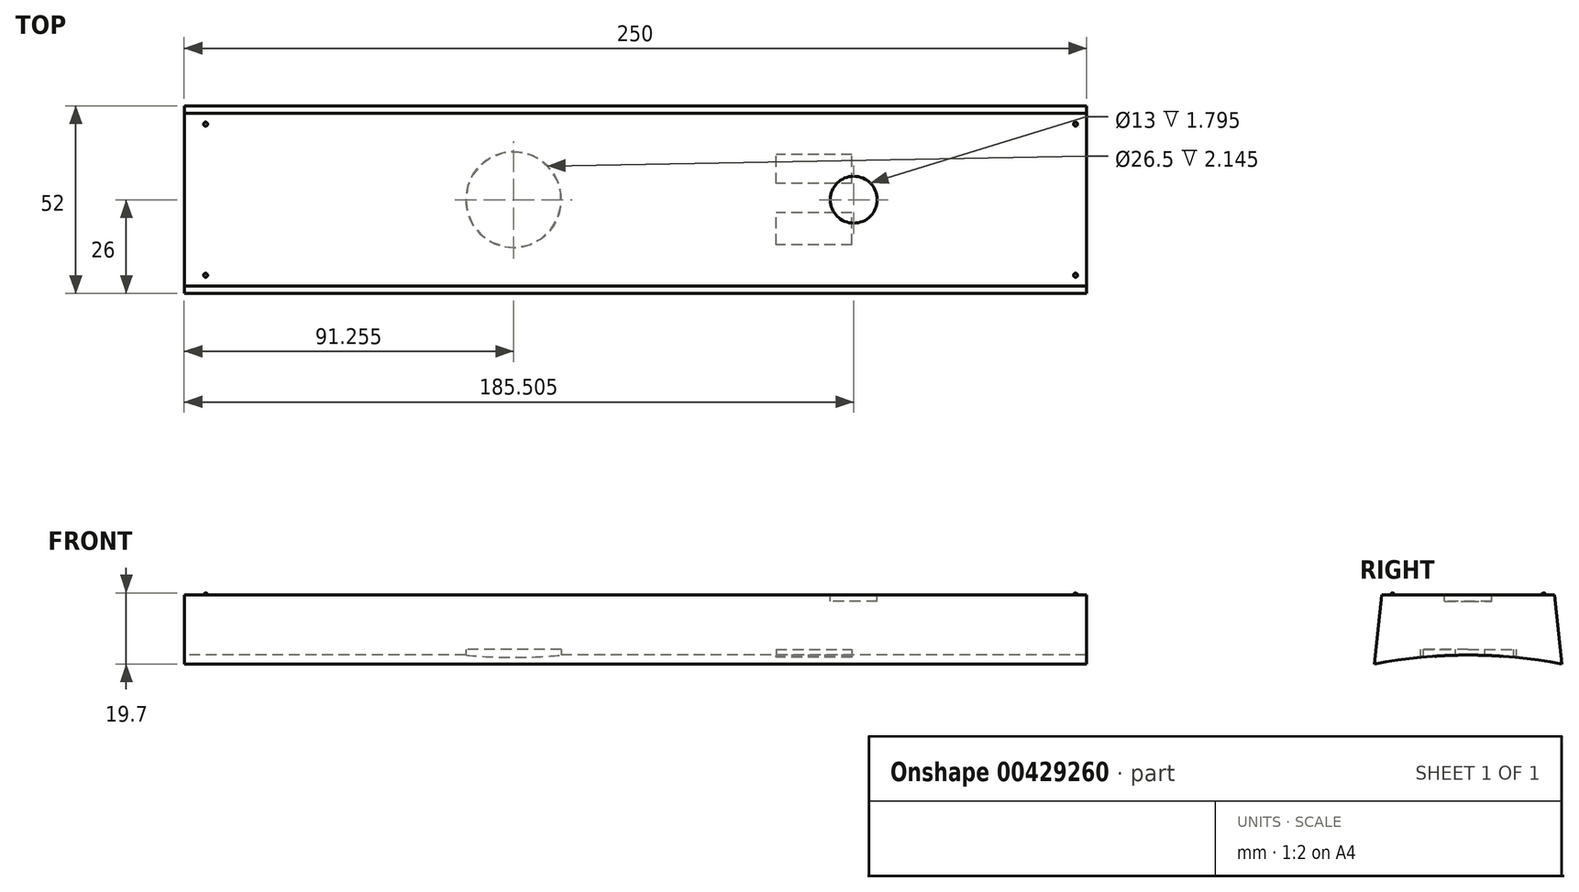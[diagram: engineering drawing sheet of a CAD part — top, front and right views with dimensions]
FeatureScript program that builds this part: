
annotation { "Feature Type Name" : "Feature", "Feature Type Description" : "" }
export const myFeature = defineFeature(function(context is Context, id is Id, definition is map)
    precondition{}
    {
        {
            var Q0;
            Q0=qCreatedBy(makeId("Top.planeOp"),FACE);
            var sketch = newSketch(context, id + "F0", { "sketchPlane" : qUnion([Q0])});
            skLineSegment(sketch, "E0.bottom", {"start": v(-126.45, 52) * mm, "end": v(123.55, 52) * mm});
            skLineSegment(sketch, "E0.top", {"start": v(-126.45, 0) * mm, "end": v(123.55, 0) * mm});
            skLineSegment(sketch, "E0.left", {"start": v(-126.45, 52) * mm, "end": v(-126.45, 0) * mm});
            skLineSegment(sketch, "E0.right", {"start": v(123.55, 52) * mm, "end": v(123.55, 0) * mm});
            skSolve(sketch);
        }
        {
            var Q0;
            Q0 = qSketchRegion(id + "F0", true);
            extrude(context, id + "F1", {"entities" : qUnion([Q0]), "depth" : 19.2 * mm});
        }
        {
            var Q0;
            Q0=makeQuery(id+"F1.opExtrude","CAP_EDGE",EDGE,{"disambiguationData":[OSD([sQuery(id+"F0.wireOp",EDGE,"E0.bottom")])],"isStart":false});
            chamfer(context, id + "F2", {"entities" : qUnion([Q0]), "chamferType" : ChamferType.OFFSET_ANGLE, "width" : 19.2 * mm, "oppositeDirection" : false, "angle" : 6 * degree, "tangentPropagation" : true});
        }
        {
            var Q0;
            Q0=makeQuery(id+"F1.opExtrude","CAP_EDGE",EDGE,{"disambiguationData":[OSD([sQuery(id+"F0.wireOp",EDGE,"E0.top")])],"isStart":false});
            chamfer(context, id + "F3", {"entities" : qUnion([Q0]), "chamferType" : ChamferType.OFFSET_ANGLE, "width" : 19.2 * mm, "oppositeDirection" : true, "angle" : 6 * degree, "tangentPropagation" : true});
        }
        {
            var Q0;
            Q0=makeQuery(id+"F1.opExtrude","CAP_FACE",FACE,{"disambiguationData":[OSD([sQuery(id+"F0.wireOp",EDGE,"E0.bottom"),sQuery(id+"F0.wireOp",EDGE,"E0.top"),sQuery(id+"F0.wireOp",EDGE,"E0.left"),sQuery(id+"F0.wireOp",EDGE,"E0.right")])],"isStart":false});
            var sketch = newSketch(context, id + "F4", { "sketchPlane" : qUnion([Q0])});
            skCircle(sketch, "E1", {"center": v(59.05, 26) * mm, "radius": 6.5 * mm});
            skSolve(sketch);
        }
        {
            var Q0;
            Q0 = qSketchRegion(id + "F4", true);
            extrude(context, id + "F5", {"entities" : qUnion([Q0]), "operationType" : NewBodyOperationType.REMOVE, "oppositeDirection" : true, "depth" : 1.8 * mm});
        }
        {
            var Q0;
            Q0=makeQuery(id+"F1.opExtrude","SWEPT_FACE",FACE,{"disambiguationData":[OSD([sQuery(id+"F0.wireOp",EDGE,"E0.right")])]});
            var sketch = newSketch(context, id + "F6", { "sketchPlane" : qUnion([Q0])});
            skArc(sketch, "E2", {"start": v(52, 0) * mm, "mid": v(26, 2.5) * mm, "end": v(0, 0) * mm});
            skLineSegment(sketch, "E3", {"start": v(0, 0) * mm, "end": v(-4.1, -9.83) * mm});
            skLineSegment(sketch, "E4", {"start": v(-4.1, -9.83) * mm, "end": v(56.27, -9.83) * mm});
            skLineSegment(sketch, "E5", {"start": v(56.27, -9.83) * mm, "end": v(52, 0) * mm});
            skSolve(sketch);
        }
        {
            var Q0;
            Q0=makeQuery(id+"F6.imprint","IMPRINT",FACE,{"disambiguationData":[TD([[makeQuery(id+"F6.imprint","IMPRINT",EDGE,{"derivedFrom":sQuery(id+"F6.wireOp",EDGE,"E3")}),1.0]])]});
            var Q1;
            Q1=makeQuery(id+"F6.imprint","IMPRINT",FACE,{"disambiguationData":[TD([[makeQuery(id+"F6.imprint","IMPRINT",EDGE,{"derivedFrom":sQuery(id+"F6.wireOp",EDGE,"E2")}),1.0]])]});
            extrude(context, id + "F7", {"entities" : qUnion([Q0, Q1]), "operationType" : NewBodyOperationType.REMOVE, "depth" : 58.48 * mm, "hasSecondDirection" : true, "secondDirectionOppositeDirection" : true, "secondDirectionDepth" : 301.56 * mm});
        }
        {
            var Q0;
            Q0=makeQuery(id+"F1.opExtrude","CAP_FACE",FACE,{"disambiguationData":[OSD([sQuery(id+"F0.wireOp",EDGE,"E0.bottom"),sQuery(id+"F0.wireOp",EDGE,"E0.top"),sQuery(id+"F0.wireOp",EDGE,"E0.left"),sQuery(id+"F0.wireOp",EDGE,"E0.right")])],"isStart":false});
            var sketch = newSketch(context, id + "F8", { "sketchPlane" : qUnion([Q0])});
            skCircle(sketch, "E6", {"center": v(120.5, 5.07) * mm, "radius": 0.55 * mm});
            skCircle(sketch, "E7.MirrorC", {"center": v(120.5, 46.93) * mm, "radius": 0.55 * mm});
            skCircle(sketch, "E8.MirrorC", {"center": v(-120.5, 5.07) * mm, "radius": 0.55 * mm});
            skCircle(sketch, "E9.MirrorC", {"center": v(-120.5, 46.93) * mm, "radius": 0.55 * mm});
            skSolve(sketch);
        }
        {
            var Q0;
            Q0 = qSketchRegion(id + "F8", true);
            extrude(context, id + "F9", {"entities" : qUnion([Q0]), "operationType" : NewBodyOperationType.ADD, "depth" : 0.5 * mm});
        }
        {
            var Q0;
            Q0=makeQuery(id+"F9.opExtrude","CAP_EDGE",EDGE,{"disambiguationData":[OSD([sQuery(id+"F8.wireOp",EDGE,"E6")])],"isStart":false});
            fillet(context, id + "F10", {"entities" : qUnion([Q0]), "radius" : 0.5 * mm, "tangentPropagation" : true, "allowEdgeOverflow" : false});
        }
        {
            var Q0;
            Q0=makeQuery(id+"F9.opExtrude","CAP_EDGE",EDGE,{"disambiguationData":[OSD([sQuery(id+"F8.wireOp",EDGE,"E8.MirrorC")])],"isStart":false});
            var Q1;
            Q1=makeQuery(id+"F9.opExtrude","CAP_EDGE",EDGE,{"disambiguationData":[OSD([sQuery(id+"F8.wireOp",EDGE,"E7.MirrorC")])],"isStart":false});
            var Q2;
            Q2=makeQuery(id+"F9.opExtrude","CAP_EDGE",EDGE,{"disambiguationData":[OSD([sQuery(id+"F8.wireOp",EDGE,"E9.MirrorC")])],"isStart":false});
            fillet(context, id + "F11", {"entities" : qUnion([Q0, Q1, Q2]), "radius" : 0.5 * mm, "tangentPropagation" : true, "allowEdgeOverflow" : false});
        }
        {
            var Q0;
            Q0=qCreatedBy(makeId("Top.planeOp"),FACE);
            var sketch = newSketch(context, id + "F12", { "sketchPlane" : qUnion([Q0])});
            skCircle(sketch, "E10", {"center": v(-35.2, 26) * mm, "radius": 13.25 * mm});
            skSolve(sketch);
        }
        {
            var Q0;
            Q0 = qSketchRegion(id + "F12", true);
            extrude(context, id + "F13", {"entities" : qUnion([Q0]), "operationType" : NewBodyOperationType.REMOVE, "depth" : 4 * mm});
        }
        {
            var Q0;
            Q0=qCreatedBy(makeId("Top.planeOp"),FACE);
            var sketch = newSketch(context, id + "F14", { "sketchPlane" : qUnion([Q0])});
            skLineSegment(sketch, "E11.bottom", {"start": v(37.55, 30.5) * mm, "end": v(58.55, 30.5) * mm});
            skLineSegment(sketch, "E11.top", {"start": v(37.55, 38.5) * mm, "end": v(58.55, 38.5) * mm});
            skLineSegment(sketch, "E11.left", {"start": v(37.55, 30.5) * mm, "end": v(37.55, 38.5) * mm});
            skLineSegment(sketch, "E11.right", {"start": v(58.55, 30.5) * mm, "end": v(58.55, 38.5) * mm});
            skLineSegment(sketch, "E12.bottom", {"start": v(37.55, 13.5) * mm, "end": v(58.55, 13.5) * mm});
            skLineSegment(sketch, "E12.top", {"start": v(37.55, 22.43) * mm, "end": v(58.55, 22.43) * mm});
            skLineSegment(sketch, "E12.left", {"start": v(37.55, 13.5) * mm, "end": v(37.55, 22.43) * mm});
            skLineSegment(sketch, "E12.right", {"start": v(58.55, 13.5) * mm, "end": v(58.55, 22.43) * mm});
            skSolve(sketch);
        }
        {
            var Q0;
            Q0 = qSketchRegion(id + "F14", true);
            extrude(context, id + "F15", {"entities" : qUnion([Q0]), "operationType" : NewBodyOperationType.REMOVE, "oppositeDirection" : true, "depth" : -4 * mm});
        }
    });
